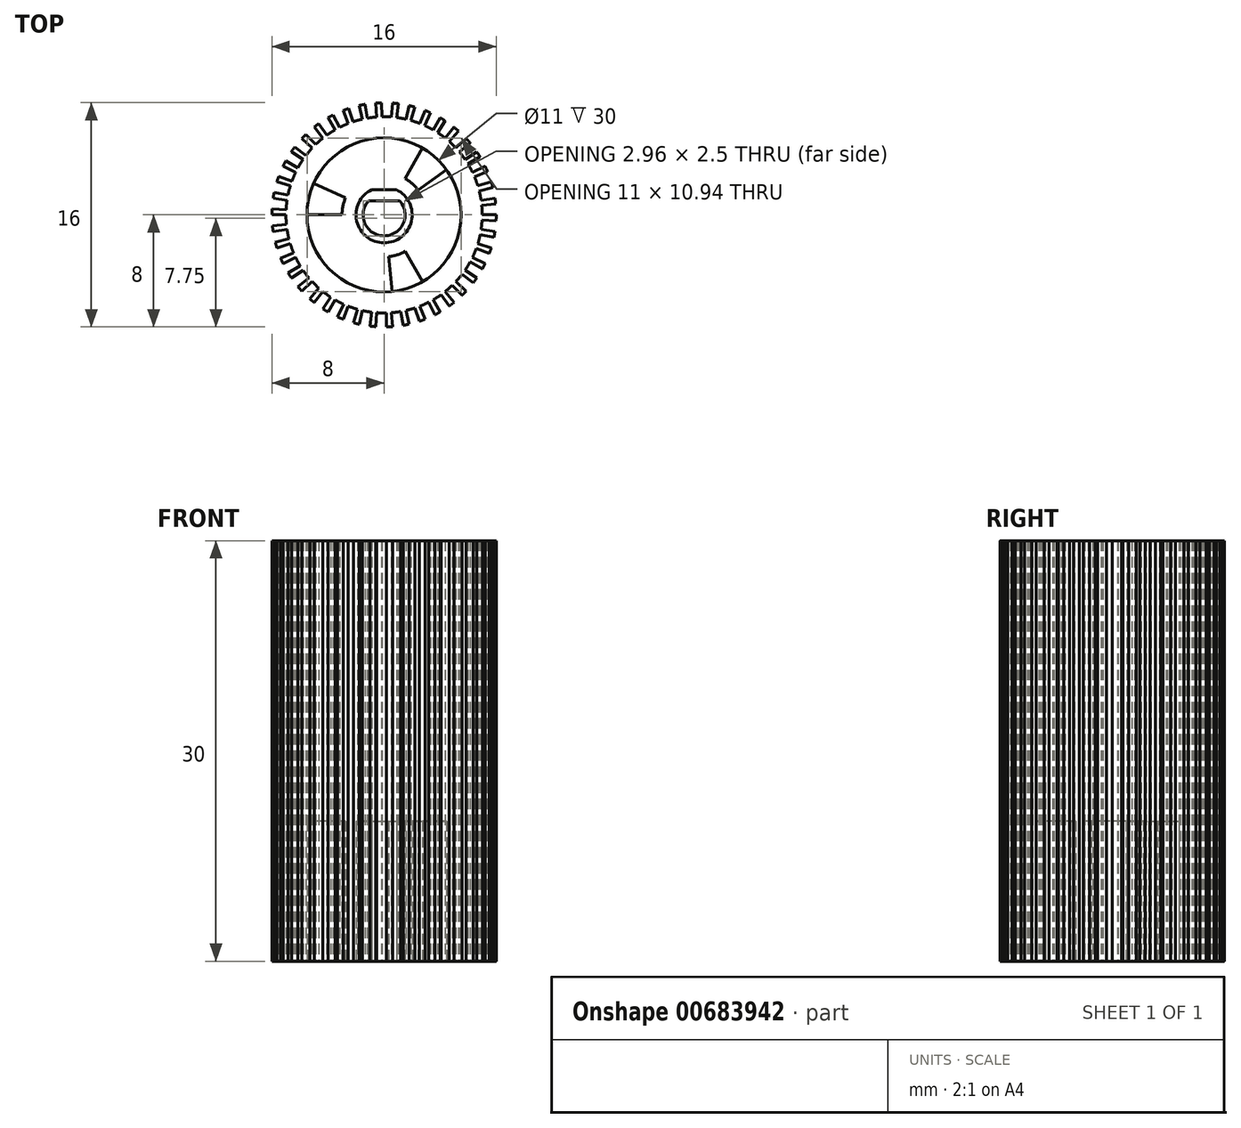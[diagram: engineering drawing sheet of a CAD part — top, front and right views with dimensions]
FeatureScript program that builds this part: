
annotation { "Feature Type Name" : "Feature", "Feature Type Description" : "" }
export const myFeature = defineFeature(function(context is Context, id is Id, definition is map)
    precondition{}
    {
        {
            var Q0;
            Q0=qCreatedBy(makeId("Top.planeOp"),FACE);
            var sketch = newSketch(context, id + "F0", { "sketchPlane" : qUnion([Q0])});
            skCircle(sketch, "E0", {"center": v(0, 0) * mm, "radius": 5.5 * mm});
            skCircle(sketch, "E1.0", {"center": v(0, 0) * mm, "radius": 7 * mm});
            skArc(sketch, "E2.0", {"start": v(-7.99, 0.42) * mm, "mid": v(-8, 0.2) * mm, "end": v(-8, 0) * mm});
            skLineSegment(sketch, "E3.trimOffspring", {"start": v(-7, 0.37) * mm, "end": v(-7.99, 0.42) * mm});
            skLineSegment(sketch, "E4.trimOffspring", {"start": v(-7, 0) * mm, "end": v(-8, 0) * mm});
            skLineSegment(sketch, "E5.1.0", {"start": v(-6.97, -0.68) * mm, "end": v(-7.96, -0.78) * mm});
            skLineSegment(sketch, "E5.1.1", {"start": v(-6.92, -1.04) * mm, "end": v(-7.91, -1.2) * mm});
            skArc(sketch, "E5.1.2", {"start": v(-7.96, -0.78) * mm, "mid": v(-7.94, -0.98) * mm, "end": v(-7.91, -1.2) * mm});
            skLineSegment(sketch, "E5.2.0", {"start": v(-6.79, -1.71) * mm, "end": v(-7.76, -1.95) * mm});
            skLineSegment(sketch, "E5.2.1", {"start": v(-6.69, -2.06) * mm, "end": v(-7.64, -2.36) * mm});
            skArc(sketch, "E5.2.2", {"start": v(-7.76, -1.95) * mm, "mid": v(-7.7, -2.16) * mm, "end": v(-7.64, -2.36) * mm});
            skLineSegment(sketch, "E5.3.0", {"start": v(-6.46, -2.7) * mm, "end": v(-7.38, -3.09) * mm});
            skLineSegment(sketch, "E5.3.1", {"start": v(-6.3, -3.04) * mm, "end": v(-7.2, -3.47) * mm});
            skArc(sketch, "E5.3.2", {"start": v(-7.38, -3.09) * mm, "mid": v(-7.3, -3.28) * mm, "end": v(-7.2, -3.47) * mm});
            skLineSegment(sketch, "E5.4.0", {"start": v(-5.98, -3.64) * mm, "end": v(-6.84, -4.15) * mm});
            skLineSegment(sketch, "E5.4.1", {"start": v(-5.78, -3.94) * mm, "end": v(-6.6, -4.5) * mm});
            skArc(sketch, "E5.4.2", {"start": v(-6.84, -4.15) * mm, "mid": v(-6.73, -4.33) * mm, "end": v(-6.6, -4.5) * mm});
            skLineSegment(sketch, "E5.5.0", {"start": v(-5.37, -4.49) * mm, "end": v(-6.14, -5.13) * mm});
            skLineSegment(sketch, "E5.5.1", {"start": v(-5.13, -4.76) * mm, "end": v(-5.86, -5.44) * mm});
            skArc(sketch, "E5.5.2", {"start": v(-6.14, -5.13) * mm, "mid": v(-6, -5.29) * mm, "end": v(-5.86, -5.44) * mm});
            skLineSegment(sketch, "E5.6.0", {"start": v(-4.64, -5.24) * mm, "end": v(-5.3, -5.99) * mm});
            skLineSegment(sketch, "E5.6.1", {"start": v(-4.36, -5.47) * mm, "end": v(-4.99, -6.25) * mm});
            skArc(sketch, "E5.6.2", {"start": v(-5.3, -5.99) * mm, "mid": v(-5.15, -6.12) * mm, "end": v(-4.99, -6.25) * mm});
            skLineSegment(sketch, "E5.7.0", {"start": v(-3.81, -5.87) * mm, "end": v(-4.36, -6.7) * mm});
            skLineSegment(sketch, "E5.7.1", {"start": v(-3.5, -6.06) * mm, "end": v(-4, -6.93) * mm});
            skArc(sketch, "E5.7.2", {"start": v(-4.36, -6.7) * mm, "mid": v(-4.18, -6.82) * mm, "end": v(-4, -6.93) * mm});
            skLineSegment(sketch, "E5.8.0", {"start": v(-2.9, -6.37) * mm, "end": v(-3.3, -7.28) * mm});
            skLineSegment(sketch, "E5.8.1", {"start": v(-2.56, -6.52) * mm, "end": v(-2.92, -7.45) * mm});
            skArc(sketch, "E5.8.2", {"start": v(-3.3, -7.28) * mm, "mid": v(-3.12, -7.37) * mm, "end": v(-2.92, -7.45) * mm});
            skLineSegment(sketch, "E5.9.0", {"start": v(-1.91, -6.73) * mm, "end": v(-2.19, -7.7) * mm});
            skLineSegment(sketch, "E5.9.1", {"start": v(-1.56, -6.82) * mm, "end": v(-1.78, -7.8) * mm});
            skArc(sketch, "E5.9.2", {"start": v(-2.19, -7.7) * mm, "mid": v(-1.98, -7.75) * mm, "end": v(-1.78, -7.8) * mm});
            skLineSegment(sketch, "E5.10.0", {"start": v(-0.89, -6.94) * mm, "end": v(-1.01, -7.94) * mm});
            skLineSegment(sketch, "E5.10.1", {"start": v(-0.52, -6.98) * mm, "end": v(-0.6, -7.98) * mm});
            skArc(sketch, "E5.10.2", {"start": v(-1.01, -7.94) * mm, "mid": v(-0.8, -7.96) * mm, "end": v(-0.6, -7.98) * mm});
            skLineSegment(sketch, "E5.11.0", {"start": v(0.16, -7) * mm, "end": v(0.18, -8) * mm});
            skLineSegment(sketch, "E5.11.1", {"start": v(0.52, -6.98) * mm, "end": v(0.6, -7.98) * mm});
            skArc(sketch, "E5.11.2", {"start": v(0.18, -8) * mm, "mid": v(0.39, -8) * mm, "end": v(0.6, -7.98) * mm});
            skLineSegment(sketch, "E5.12.0", {"start": v(1.2, -6.9) * mm, "end": v(1.37, -7.88) * mm});
            skLineSegment(sketch, "E5.12.1", {"start": v(1.56, -6.82) * mm, "end": v(1.78, -7.8) * mm});
            skArc(sketch, "E5.12.2", {"start": v(1.37, -7.88) * mm, "mid": v(1.58, -7.84) * mm, "end": v(1.78, -7.8) * mm});
            skLineSegment(sketch, "E5.13.0", {"start": v(2.21, -6.64) * mm, "end": v(2.53, -7.59) * mm});
            skLineSegment(sketch, "E5.13.1", {"start": v(2.56, -6.52) * mm, "end": v(2.92, -7.45) * mm});
            skArc(sketch, "E5.13.2", {"start": v(2.53, -7.59) * mm, "mid": v(2.73, -7.52) * mm, "end": v(2.92, -7.45) * mm});
            skLineSegment(sketch, "E5.14.0", {"start": v(3.18, -6.24) * mm, "end": v(3.63, -7.13) * mm});
            skLineSegment(sketch, "E5.14.1", {"start": v(3.5, -6.06) * mm, "end": v(4, -6.93) * mm});
            skArc(sketch, "E5.14.2", {"start": v(3.63, -7.13) * mm, "mid": v(3.82, -7.03) * mm, "end": v(4, -6.93) * mm});
            skLineSegment(sketch, "E5.15.0", {"start": v(4.07, -5.7) * mm, "end": v(4.65, -6.5) * mm});
            skLineSegment(sketch, "E5.15.1", {"start": v(4.36, -5.47) * mm, "end": v(4.99, -6.25) * mm});
            skArc(sketch, "E5.15.2", {"start": v(4.65, -6.5) * mm, "mid": v(4.82, -6.38) * mm, "end": v(4.99, -6.25) * mm});
            skLineSegment(sketch, "E5.16.0", {"start": v(4.88, -5.02) * mm, "end": v(5.57, -5.74) * mm});
            skLineSegment(sketch, "E5.16.1", {"start": v(5.13, -4.76) * mm, "end": v(5.86, -5.44) * mm});
            skArc(sketch, "E5.16.2", {"start": v(5.57, -5.74) * mm, "mid": v(5.72, -5.6) * mm, "end": v(5.86, -5.44) * mm});
            skLineSegment(sketch, "E5.17.0", {"start": v(5.57, -4.24) * mm, "end": v(6.36, -4.85) * mm});
            skLineSegment(sketch, "E5.17.1", {"start": v(5.78, -3.94) * mm, "end": v(6.6, -4.5) * mm});
            skArc(sketch, "E5.17.2", {"start": v(6.36, -4.85) * mm, "mid": v(6.49, -4.68) * mm, "end": v(6.6, -4.5) * mm});
            skLineSegment(sketch, "E5.18.0", {"start": v(6.14, -3.36) * mm, "end": v(7.02, -3.84) * mm});
            skLineSegment(sketch, "E5.18.1", {"start": v(6.3, -3.04) * mm, "end": v(7.2, -3.47) * mm});
            skArc(sketch, "E5.18.2", {"start": v(7.02, -3.84) * mm, "mid": v(7.11, -3.66) * mm, "end": v(7.2, -3.47) * mm});
            skLineSegment(sketch, "E5.19.0", {"start": v(6.57, -2.41) * mm, "end": v(7.51, -2.75) * mm});
            skLineSegment(sketch, "E5.19.1", {"start": v(6.69, -2.06) * mm, "end": v(7.64, -2.36) * mm});
            skArc(sketch, "E5.19.2", {"start": v(7.51, -2.75) * mm, "mid": v(7.58, -2.56) * mm, "end": v(7.64, -2.36) * mm});
            skLineSegment(sketch, "E5.20.0", {"start": v(6.86, -1.4) * mm, "end": v(7.84, -1.6) * mm});
            skLineSegment(sketch, "E5.20.1", {"start": v(6.92, -1.04) * mm, "end": v(7.91, -1.2) * mm});
            skArc(sketch, "E5.20.2", {"start": v(7.84, -1.6) * mm, "mid": v(7.88, -1.4) * mm, "end": v(7.91, -1.2) * mm});
            skLineSegment(sketch, "E5.21.0", {"start": v(7, -0.37) * mm, "end": v(7.99, -0.42) * mm});
            skLineSegment(sketch, "E5.21.1", {"start": v(7, 0) * mm, "end": v(8, 0) * mm});
            skArc(sketch, "E5.21.2", {"start": v(7.99, -0.42) * mm, "mid": v(8, -0.2) * mm, "end": v(8, 0) * mm});
            skLineSegment(sketch, "E5.22.0", {"start": v(6.97, 0.68) * mm, "end": v(7.96, 0.78) * mm});
            skLineSegment(sketch, "E5.22.1", {"start": v(6.92, 1.04) * mm, "end": v(7.91, 1.2) * mm});
            skArc(sketch, "E5.22.2", {"start": v(7.96, 0.78) * mm, "mid": v(7.94, 0.98) * mm, "end": v(7.91, 1.2) * mm});
            skLineSegment(sketch, "E5.23.0", {"start": v(6.79, 1.71) * mm, "end": v(7.76, 1.95) * mm});
            skLineSegment(sketch, "E5.23.1", {"start": v(6.69, 2.06) * mm, "end": v(7.64, 2.36) * mm});
            skArc(sketch, "E5.23.2", {"start": v(7.76, 1.95) * mm, "mid": v(7.7, 2.16) * mm, "end": v(7.64, 2.36) * mm});
            skLineSegment(sketch, "E5.24.0", {"start": v(6.46, 2.7) * mm, "end": v(7.38, 3.09) * mm});
            skLineSegment(sketch, "E5.24.1", {"start": v(6.3, 3.04) * mm, "end": v(7.2, 3.47) * mm});
            skArc(sketch, "E5.24.2", {"start": v(7.38, 3.09) * mm, "mid": v(7.3, 3.28) * mm, "end": v(7.2, 3.47) * mm});
            skLineSegment(sketch, "E5.25.0", {"start": v(5.98, 3.64) * mm, "end": v(6.84, 4.15) * mm});
            skLineSegment(sketch, "E5.25.1", {"start": v(5.78, 3.94) * mm, "end": v(6.6, 4.5) * mm});
            skArc(sketch, "E5.25.2", {"start": v(6.84, 4.15) * mm, "mid": v(6.73, 4.33) * mm, "end": v(6.6, 4.5) * mm});
            skLineSegment(sketch, "E5.26.0", {"start": v(5.37, 4.49) * mm, "end": v(6.14, 5.13) * mm});
            skLineSegment(sketch, "E5.26.1", {"start": v(5.13, 4.76) * mm, "end": v(5.86, 5.44) * mm});
            skArc(sketch, "E5.26.2", {"start": v(6.14, 5.13) * mm, "mid": v(6, 5.29) * mm, "end": v(5.86, 5.44) * mm});
            skLineSegment(sketch, "E5.27.0", {"start": v(4.64, 5.24) * mm, "end": v(5.3, 5.99) * mm});
            skLineSegment(sketch, "E5.27.1", {"start": v(4.36, 5.47) * mm, "end": v(4.99, 6.25) * mm});
            skArc(sketch, "E5.27.2", {"start": v(5.3, 5.99) * mm, "mid": v(5.15, 6.12) * mm, "end": v(4.99, 6.25) * mm});
            skLineSegment(sketch, "E5.28.0", {"start": v(3.81, 5.87) * mm, "end": v(4.36, 6.7) * mm});
            skLineSegment(sketch, "E5.28.1", {"start": v(3.5, 6.06) * mm, "end": v(4, 6.93) * mm});
            skArc(sketch, "E5.28.2", {"start": v(4.36, 6.7) * mm, "mid": v(4.18, 6.82) * mm, "end": v(4, 6.93) * mm});
            skLineSegment(sketch, "E5.29.0", {"start": v(2.9, 6.37) * mm, "end": v(3.3, 7.28) * mm});
            skLineSegment(sketch, "E5.29.1", {"start": v(2.56, 6.52) * mm, "end": v(2.92, 7.45) * mm});
            skArc(sketch, "E5.29.2", {"start": v(3.3, 7.28) * mm, "mid": v(3.12, 7.37) * mm, "end": v(2.92, 7.45) * mm});
            skLineSegment(sketch, "E5.30.0", {"start": v(1.91, 6.73) * mm, "end": v(2.19, 7.7) * mm});
            skLineSegment(sketch, "E5.30.1", {"start": v(1.56, 6.82) * mm, "end": v(1.78, 7.8) * mm});
            skArc(sketch, "E5.30.2", {"start": v(2.19, 7.7) * mm, "mid": v(1.98, 7.75) * mm, "end": v(1.78, 7.8) * mm});
            skLineSegment(sketch, "E5.31.0", {"start": v(0.89, 6.94) * mm, "end": v(1.01, 7.94) * mm});
            skLineSegment(sketch, "E5.31.1", {"start": v(0.52, 6.98) * mm, "end": v(0.6, 7.98) * mm});
            skArc(sketch, "E5.31.2", {"start": v(1.01, 7.94) * mm, "mid": v(0.8, 7.96) * mm, "end": v(0.6, 7.98) * mm});
            skLineSegment(sketch, "E5.32.0", {"start": v(-0.16, 7) * mm, "end": v(-0.18, 8) * mm});
            skLineSegment(sketch, "E5.32.1", {"start": v(-0.52, 6.98) * mm, "end": v(-0.6, 7.98) * mm});
            skArc(sketch, "E5.32.2", {"start": v(-0.18, 8) * mm, "mid": v(-0.39, 8) * mm, "end": v(-0.6, 7.98) * mm});
            skLineSegment(sketch, "E5.33.0", {"start": v(-1.2, 6.9) * mm, "end": v(-1.37, 7.88) * mm});
            skLineSegment(sketch, "E5.33.1", {"start": v(-1.56, 6.82) * mm, "end": v(-1.78, 7.8) * mm});
            skArc(sketch, "E5.33.2", {"start": v(-1.37, 7.88) * mm, "mid": v(-1.58, 7.84) * mm, "end": v(-1.78, 7.8) * mm});
            skLineSegment(sketch, "E5.34.0", {"start": v(-2.21, 6.64) * mm, "end": v(-2.53, 7.59) * mm});
            skLineSegment(sketch, "E5.34.1", {"start": v(-2.56, 6.52) * mm, "end": v(-2.92, 7.45) * mm});
            skArc(sketch, "E5.34.2", {"start": v(-2.53, 7.59) * mm, "mid": v(-2.73, 7.52) * mm, "end": v(-2.92, 7.45) * mm});
            skLineSegment(sketch, "E5.35.0", {"start": v(-3.18, 6.24) * mm, "end": v(-3.63, 7.13) * mm});
            skLineSegment(sketch, "E5.35.1", {"start": v(-3.5, 6.06) * mm, "end": v(-4, 6.93) * mm});
            skArc(sketch, "E5.35.2", {"start": v(-3.63, 7.13) * mm, "mid": v(-3.82, 7.03) * mm, "end": v(-4, 6.93) * mm});
            skLineSegment(sketch, "E5.36.0", {"start": v(-4.07, 5.7) * mm, "end": v(-4.65, 6.5) * mm});
            skLineSegment(sketch, "E5.36.1", {"start": v(-4.36, 5.47) * mm, "end": v(-4.99, 6.25) * mm});
            skArc(sketch, "E5.36.2", {"start": v(-4.65, 6.5) * mm, "mid": v(-4.82, 6.38) * mm, "end": v(-4.99, 6.25) * mm});
            skLineSegment(sketch, "E5.37.0", {"start": v(-4.88, 5.02) * mm, "end": v(-5.57, 5.74) * mm});
            skLineSegment(sketch, "E5.37.1", {"start": v(-5.13, 4.76) * mm, "end": v(-5.86, 5.44) * mm});
            skArc(sketch, "E5.37.2", {"start": v(-5.57, 5.74) * mm, "mid": v(-5.72, 5.6) * mm, "end": v(-5.86, 5.44) * mm});
            skLineSegment(sketch, "E5.38.0", {"start": v(-5.57, 4.24) * mm, "end": v(-6.36, 4.85) * mm});
            skLineSegment(sketch, "E5.38.1", {"start": v(-5.78, 3.94) * mm, "end": v(-6.6, 4.5) * mm});
            skArc(sketch, "E5.38.2", {"start": v(-6.36, 4.85) * mm, "mid": v(-6.49, 4.68) * mm, "end": v(-6.6, 4.5) * mm});
            skLineSegment(sketch, "E5.39.0", {"start": v(-6.14, 3.36) * mm, "end": v(-7.02, 3.84) * mm});
            skLineSegment(sketch, "E5.39.1", {"start": v(-6.3, 3.04) * mm, "end": v(-7.2, 3.47) * mm});
            skArc(sketch, "E5.39.2", {"start": v(-7.02, 3.84) * mm, "mid": v(-7.11, 3.66) * mm, "end": v(-7.2, 3.47) * mm});
            skLineSegment(sketch, "E5.40.0", {"start": v(-6.57, 2.41) * mm, "end": v(-7.51, 2.75) * mm});
            skLineSegment(sketch, "E5.40.1", {"start": v(-6.69, 2.06) * mm, "end": v(-7.64, 2.36) * mm});
            skArc(sketch, "E5.40.2", {"start": v(-7.51, 2.75) * mm, "mid": v(-7.58, 2.56) * mm, "end": v(-7.64, 2.36) * mm});
            skLineSegment(sketch, "E5.41.0", {"start": v(-6.86, 1.4) * mm, "end": v(-7.84, 1.6) * mm});
            skLineSegment(sketch, "E5.41.1", {"start": v(-6.92, 1.04) * mm, "end": v(-7.91, 1.2) * mm});
            skArc(sketch, "E5.41.2", {"start": v(-7.84, 1.6) * mm, "mid": v(-7.88, 1.4) * mm, "end": v(-7.91, 1.2) * mm});
            skArc(sketch, "E6", {"start": v(-1.12, 1) * mm, "mid": v(0, -1.5) * mm, "end": v(1.12, 1) * mm});
            skLineSegment(sketch, "E7", {"start": v(-1.12, 1) * mm, "end": v(1.12, 1) * mm});
            skCircle(sketch, "E8.0", {"center": v(0, 0) * mm, "radius": 3 * mm});
            skLineSegment(sketch, "E9.trimOffspring", {"start": v(-2.74, 1.22) * mm, "end": v(-5.02, 2.24) * mm});
            skLineSegment(sketch, "E10.trimOffspring", {"start": v(-3, 0) * mm, "end": v(-5.5, 0) * mm});
            skLineSegment(sketch, "E11.1.0", {"start": v(0.31, -2.98) * mm, "end": v(0.57, -5.47) * mm});
            skLineSegment(sketch, "E11.1.1", {"start": v(1.5, -2.6) * mm, "end": v(2.75, -4.76) * mm});
            skLineSegment(sketch, "E11.2.0", {"start": v(2.43, 1.76) * mm, "end": v(4.45, 3.23) * mm});
            skLineSegment(sketch, "E11.2.1", {"start": v(1.5, 2.6) * mm, "end": v(2.75, 4.76) * mm});
            skCircle(sketch, "E12", {"center": v(0, 0) * mm, "radius": 2 * mm});
            skLineSegment(sketch, "E13", {"start": v(-0.88, 1.8) * mm, "end": v(0.88, 1.8) * mm});
            skSolve(sketch);
        }
        {
            var Q0;
            {var subQ0=sQuery(id+"F0.wireOp",EDGE,"E10.trimOffspring");Q0=makeQuery(id+"F0.imprint","IMPRINT",FACE,{"disambiguationData":[TD([[makeQuery(id+"F0.imprint","IMPRINT",EDGE,{"derivedFrom":subQ0}),1.0]])]});}
            var Q1;
            {var subQ0=sQuery(id+"F0.wireOp",EDGE,"E9.trimOffspring");Q1=makeQuery(id+"F0.imprint","IMPRINT",FACE,{"disambiguationData":[TD([[makeQuery(id+"F0.imprint","IMPRINT",EDGE,{"derivedFrom":subQ0}),1.0]])]});}
            var Q2;
            {var subQ0=sQuery(id+"F0.wireOp",EDGE,"E9.trimOffspring");Q2=makeQuery(id+"F0.imprint","IMPRINT",FACE,{"disambiguationData":[TD([[makeQuery(id+"F0.imprint","IMPRINT",EDGE,{"derivedFrom":subQ0}),-1.0]])]});}
            var Q3;
            {var subQ0=sQuery(id+"F0.wireOp",EDGE,"E11.2.0");Q3=makeQuery(id+"F0.imprint","IMPRINT",FACE,{"disambiguationData":[TD([[makeQuery(id+"F0.imprint","IMPRINT",EDGE,{"derivedFrom":subQ0}),1.0]])]});}
            var Q4;
            {var subQ0=sQuery(id+"F0.wireOp",EDGE,"E11.1.1");Q4=makeQuery(id+"F0.imprint","IMPRINT",FACE,{"disambiguationData":[TD([[makeQuery(id+"F0.imprint","IMPRINT",EDGE,{"derivedFrom":subQ0}),1.0]])]});}
            var Q5;
            {var subQ0=sQuery(id+"F0.wireOp",EDGE,"E11.1.0");Q5=makeQuery(id+"F0.imprint","IMPRINT",FACE,{"disambiguationData":[TD([[makeQuery(id+"F0.imprint","IMPRINT",EDGE,{"derivedFrom":subQ0}),1.0]])]});}
            extrude(context, id + "F1", {"entities" : qUnion([Q0, Q1, Q2, Q3, Q4, Q5]), "depth" : 1.5 * mm, "offsetDistance" : 25 * mm});
        }
        {
            var Q0;
            {var subQ31=sQuery(id+"F0.wireOp",EDGE,"E0");var subQ33=makeQuery(id+"F0.imprint","INTERSECT",VERTEX,{"derivedFrom":[subQ31,sQuery(id+"F0.wireOp",EDGE,"E11.2.0")]});Q0=makeQuery(id+"F0.imprint","IMPRINT",FACE,{"disambiguationData":[TD([[makeQuery(id+"F0.imprint","IMPRINT",EDGE,{"disambiguationData":[TD([[subQ33,-1.0]])],"derivedFrom":subQ31}),-1.0]])]});}
            var Q1;
            {var subQ0=sQuery(id+"F0.wireOp",EDGE,"E5.38.0");Q1=makeQuery(id+"F0.imprint","IMPRINT",FACE,{"disambiguationData":[TD([[makeQuery(id+"F0.imprint","IMPRINT",EDGE,{"derivedFrom":subQ0}),1.0]])]});}
            var Q2;
            {var subQ0=sQuery(id+"F0.wireOp",EDGE,"E5.37.0");Q2=makeQuery(id+"F0.imprint","IMPRINT",FACE,{"disambiguationData":[TD([[makeQuery(id+"F0.imprint","IMPRINT",EDGE,{"derivedFrom":subQ0}),1.0]])]});}
            var Q3;
            {var subQ0=sQuery(id+"F0.wireOp",EDGE,"E5.36.0");Q3=makeQuery(id+"F0.imprint","IMPRINT",FACE,{"disambiguationData":[TD([[makeQuery(id+"F0.imprint","IMPRINT",EDGE,{"derivedFrom":subQ0}),1.0]])]});}
            var Q4;
            {var subQ0=sQuery(id+"F0.wireOp",EDGE,"E5.35.0");Q4=makeQuery(id+"F0.imprint","IMPRINT",FACE,{"disambiguationData":[TD([[makeQuery(id+"F0.imprint","IMPRINT",EDGE,{"derivedFrom":subQ0}),1.0]])]});}
            var Q5;
            {var subQ0=sQuery(id+"F0.wireOp",EDGE,"E5.34.0");Q5=makeQuery(id+"F0.imprint","IMPRINT",FACE,{"disambiguationData":[TD([[makeQuery(id+"F0.imprint","IMPRINT",EDGE,{"derivedFrom":subQ0}),1.0]])]});}
            var Q6;
            {var subQ0=sQuery(id+"F0.wireOp",EDGE,"E5.33.0");Q6=makeQuery(id+"F0.imprint","IMPRINT",FACE,{"disambiguationData":[TD([[makeQuery(id+"F0.imprint","IMPRINT",EDGE,{"derivedFrom":subQ0}),1.0]])]});}
            var Q7;
            {var subQ0=sQuery(id+"F0.wireOp",EDGE,"E5.32.0");Q7=makeQuery(id+"F0.imprint","IMPRINT",FACE,{"disambiguationData":[TD([[makeQuery(id+"F0.imprint","IMPRINT",EDGE,{"derivedFrom":subQ0}),1.0]])]});}
            var Q8;
            {var subQ0=sQuery(id+"F0.wireOp",EDGE,"E5.31.0");Q8=makeQuery(id+"F0.imprint","IMPRINT",FACE,{"disambiguationData":[TD([[makeQuery(id+"F0.imprint","IMPRINT",EDGE,{"derivedFrom":subQ0}),1.0]])]});}
            var Q9;
            {var subQ0=sQuery(id+"F0.wireOp",EDGE,"E5.30.0");Q9=makeQuery(id+"F0.imprint","IMPRINT",FACE,{"disambiguationData":[TD([[makeQuery(id+"F0.imprint","IMPRINT",EDGE,{"derivedFrom":subQ0}),1.0]])]});}
            var Q10;
            {var subQ0=sQuery(id+"F0.wireOp",EDGE,"E5.29.0");Q10=makeQuery(id+"F0.imprint","IMPRINT",FACE,{"disambiguationData":[TD([[makeQuery(id+"F0.imprint","IMPRINT",EDGE,{"derivedFrom":subQ0}),1.0]])]});}
            var Q11;
            {var subQ0=sQuery(id+"F0.wireOp",EDGE,"E5.28.0");Q11=makeQuery(id+"F0.imprint","IMPRINT",FACE,{"disambiguationData":[TD([[makeQuery(id+"F0.imprint","IMPRINT",EDGE,{"derivedFrom":subQ0}),1.0]])]});}
            var Q12;
            {var subQ0=sQuery(id+"F0.wireOp",EDGE,"E5.27.0");Q12=makeQuery(id+"F0.imprint","IMPRINT",FACE,{"disambiguationData":[TD([[makeQuery(id+"F0.imprint","IMPRINT",EDGE,{"derivedFrom":subQ0}),1.0]])]});}
            var Q13;
            {var subQ0=sQuery(id+"F0.wireOp",EDGE,"E5.26.0");Q13=makeQuery(id+"F0.imprint","IMPRINT",FACE,{"disambiguationData":[TD([[makeQuery(id+"F0.imprint","IMPRINT",EDGE,{"derivedFrom":subQ0}),1.0]])]});}
            var Q14;
            {var subQ0=sQuery(id+"F0.wireOp",EDGE,"E5.25.0");Q14=makeQuery(id+"F0.imprint","IMPRINT",FACE,{"disambiguationData":[TD([[makeQuery(id+"F0.imprint","IMPRINT",EDGE,{"derivedFrom":subQ0}),1.0]])]});}
            var Q15;
            {var subQ0=sQuery(id+"F0.wireOp",EDGE,"E5.24.0");Q15=makeQuery(id+"F0.imprint","IMPRINT",FACE,{"disambiguationData":[TD([[makeQuery(id+"F0.imprint","IMPRINT",EDGE,{"derivedFrom":subQ0}),1.0]])]});}
            var Q16;
            {var subQ0=sQuery(id+"F0.wireOp",EDGE,"E5.23.0");Q16=makeQuery(id+"F0.imprint","IMPRINT",FACE,{"disambiguationData":[TD([[makeQuery(id+"F0.imprint","IMPRINT",EDGE,{"derivedFrom":subQ0}),1.0]])]});}
            var Q17;
            {var subQ0=sQuery(id+"F0.wireOp",EDGE,"E5.22.0");Q17=makeQuery(id+"F0.imprint","IMPRINT",FACE,{"disambiguationData":[TD([[makeQuery(id+"F0.imprint","IMPRINT",EDGE,{"derivedFrom":subQ0}),1.0]])]});}
            var Q18;
            {var subQ0=sQuery(id+"F0.wireOp",EDGE,"E5.21.0");Q18=makeQuery(id+"F0.imprint","IMPRINT",FACE,{"disambiguationData":[TD([[makeQuery(id+"F0.imprint","IMPRINT",EDGE,{"derivedFrom":subQ0}),1.0]])]});}
            var Q19;
            {var subQ0=sQuery(id+"F0.wireOp",EDGE,"E5.20.0");Q19=makeQuery(id+"F0.imprint","IMPRINT",FACE,{"disambiguationData":[TD([[makeQuery(id+"F0.imprint","IMPRINT",EDGE,{"derivedFrom":subQ0}),1.0]])]});}
            var Q20;
            {var subQ0=sQuery(id+"F0.wireOp",EDGE,"E5.19.0");Q20=makeQuery(id+"F0.imprint","IMPRINT",FACE,{"disambiguationData":[TD([[makeQuery(id+"F0.imprint","IMPRINT",EDGE,{"derivedFrom":subQ0}),1.0]])]});}
            var Q21;
            {var subQ0=sQuery(id+"F0.wireOp",EDGE,"E5.18.0");Q21=makeQuery(id+"F0.imprint","IMPRINT",FACE,{"disambiguationData":[TD([[makeQuery(id+"F0.imprint","IMPRINT",EDGE,{"derivedFrom":subQ0}),1.0]])]});}
            var Q22;
            {var subQ0=sQuery(id+"F0.wireOp",EDGE,"E5.17.0");Q22=makeQuery(id+"F0.imprint","IMPRINT",FACE,{"disambiguationData":[TD([[makeQuery(id+"F0.imprint","IMPRINT",EDGE,{"derivedFrom":subQ0}),1.0]])]});}
            var Q23;
            {var subQ0=sQuery(id+"F0.wireOp",EDGE,"E5.16.0");Q23=makeQuery(id+"F0.imprint","IMPRINT",FACE,{"disambiguationData":[TD([[makeQuery(id+"F0.imprint","IMPRINT",EDGE,{"derivedFrom":subQ0}),1.0]])]});}
            var Q24;
            {var subQ0=sQuery(id+"F0.wireOp",EDGE,"E5.15.0");Q24=makeQuery(id+"F0.imprint","IMPRINT",FACE,{"disambiguationData":[TD([[makeQuery(id+"F0.imprint","IMPRINT",EDGE,{"derivedFrom":subQ0}),1.0]])]});}
            var Q25;
            {var subQ0=sQuery(id+"F0.wireOp",EDGE,"E5.14.0");Q25=makeQuery(id+"F0.imprint","IMPRINT",FACE,{"disambiguationData":[TD([[makeQuery(id+"F0.imprint","IMPRINT",EDGE,{"derivedFrom":subQ0}),1.0]])]});}
            var Q26;
            {var subQ0=sQuery(id+"F0.wireOp",EDGE,"E5.13.0");Q26=makeQuery(id+"F0.imprint","IMPRINT",FACE,{"disambiguationData":[TD([[makeQuery(id+"F0.imprint","IMPRINT",EDGE,{"derivedFrom":subQ0}),1.0]])]});}
            var Q27;
            {var subQ0=sQuery(id+"F0.wireOp",EDGE,"E5.12.0");Q27=makeQuery(id+"F0.imprint","IMPRINT",FACE,{"disambiguationData":[TD([[makeQuery(id+"F0.imprint","IMPRINT",EDGE,{"derivedFrom":subQ0}),1.0]])]});}
            var Q28;
            {var subQ0=sQuery(id+"F0.wireOp",EDGE,"E5.11.0");Q28=makeQuery(id+"F0.imprint","IMPRINT",FACE,{"disambiguationData":[TD([[makeQuery(id+"F0.imprint","IMPRINT",EDGE,{"derivedFrom":subQ0}),1.0]])]});}
            var Q29;
            {var subQ0=sQuery(id+"F0.wireOp",EDGE,"E5.10.0");Q29=makeQuery(id+"F0.imprint","IMPRINT",FACE,{"disambiguationData":[TD([[makeQuery(id+"F0.imprint","IMPRINT",EDGE,{"derivedFrom":subQ0}),1.0]])]});}
            var Q30;
            {var subQ0=sQuery(id+"F0.wireOp",EDGE,"E5.9.0");Q30=makeQuery(id+"F0.imprint","IMPRINT",FACE,{"disambiguationData":[TD([[makeQuery(id+"F0.imprint","IMPRINT",EDGE,{"derivedFrom":subQ0}),1.0]])]});}
            var Q31;
            {var subQ0=sQuery(id+"F0.wireOp",EDGE,"E5.8.0");Q31=makeQuery(id+"F0.imprint","IMPRINT",FACE,{"disambiguationData":[TD([[makeQuery(id+"F0.imprint","IMPRINT",EDGE,{"derivedFrom":subQ0}),1.0]])]});}
            var Q32;
            {var subQ0=sQuery(id+"F0.wireOp",EDGE,"E5.7.0");Q32=makeQuery(id+"F0.imprint","IMPRINT",FACE,{"disambiguationData":[TD([[makeQuery(id+"F0.imprint","IMPRINT",EDGE,{"derivedFrom":subQ0}),1.0]])]});}
            var Q33;
            {var subQ0=sQuery(id+"F0.wireOp",EDGE,"E5.6.0");Q33=makeQuery(id+"F0.imprint","IMPRINT",FACE,{"disambiguationData":[TD([[makeQuery(id+"F0.imprint","IMPRINT",EDGE,{"derivedFrom":subQ0}),1.0]])]});}
            var Q34;
            {var subQ0=sQuery(id+"F0.wireOp",EDGE,"E5.5.0");Q34=makeQuery(id+"F0.imprint","IMPRINT",FACE,{"disambiguationData":[TD([[makeQuery(id+"F0.imprint","IMPRINT",EDGE,{"derivedFrom":subQ0}),1.0]])]});}
            var Q35;
            {var subQ0=sQuery(id+"F0.wireOp",EDGE,"E5.4.0");Q35=makeQuery(id+"F0.imprint","IMPRINT",FACE,{"disambiguationData":[TD([[makeQuery(id+"F0.imprint","IMPRINT",EDGE,{"derivedFrom":subQ0}),1.0]])]});}
            var Q36;
            {var subQ0=sQuery(id+"F0.wireOp",EDGE,"E5.3.0");Q36=makeQuery(id+"F0.imprint","IMPRINT",FACE,{"disambiguationData":[TD([[makeQuery(id+"F0.imprint","IMPRINT",EDGE,{"derivedFrom":subQ0}),1.0]])]});}
            var Q37;
            {var subQ0=sQuery(id+"F0.wireOp",EDGE,"E5.2.0");Q37=makeQuery(id+"F0.imprint","IMPRINT",FACE,{"disambiguationData":[TD([[makeQuery(id+"F0.imprint","IMPRINT",EDGE,{"derivedFrom":subQ0}),1.0]])]});}
            var Q38;
            {var subQ0=sQuery(id+"F0.wireOp",EDGE,"E5.1.0");Q38=makeQuery(id+"F0.imprint","IMPRINT",FACE,{"disambiguationData":[TD([[makeQuery(id+"F0.imprint","IMPRINT",EDGE,{"derivedFrom":subQ0}),1.0]])]});}
            var Q39;
            Q39=makeQuery(id+"F0.imprint","IMPRINT",FACE,{"disambiguationData":[TD([[makeQuery(id+"F0.imprint","IMPRINT",EDGE,{"derivedFrom":sQuery(id+"F0.wireOp",EDGE,"E2.0")}),1.0]])]});
            var Q40;
            {var subQ0=sQuery(id+"F0.wireOp",EDGE,"E5.41.0");Q40=makeQuery(id+"F0.imprint","IMPRINT",FACE,{"disambiguationData":[TD([[makeQuery(id+"F0.imprint","IMPRINT",EDGE,{"derivedFrom":subQ0}),1.0]])]});}
            var Q41;
            {var subQ0=sQuery(id+"F0.wireOp",EDGE,"E5.40.0");Q41=makeQuery(id+"F0.imprint","IMPRINT",FACE,{"disambiguationData":[TD([[makeQuery(id+"F0.imprint","IMPRINT",EDGE,{"derivedFrom":subQ0}),1.0]])]});}
            var Q42;
            {var subQ0=sQuery(id+"F0.wireOp",EDGE,"E5.39.0");Q42=makeQuery(id+"F0.imprint","IMPRINT",FACE,{"disambiguationData":[TD([[makeQuery(id+"F0.imprint","IMPRINT",EDGE,{"derivedFrom":subQ0}),1.0]])]});}
            extrude(context, id + "F2", {"entities" : qUnion([Q0, Q1, Q2, Q3, Q4, Q5, Q6, Q7, Q8, Q9, Q10, Q11, Q12, Q13, Q14, Q15, Q16, Q17, Q18, Q19, Q20, Q21, Q22, Q23, Q24, Q25, Q26, Q27, Q28, Q29, Q30, Q31, Q32, Q33, Q34, Q35, Q36, Q37, Q38, Q39, Q40, Q41, Q42]), "operationType" : NewBodyOperationType.ADD, "depth" : 30 * mm, "offsetDistance" : 25 * mm});
        }
        {
            var Q0;
            Q0=makeQuery(id+"F0.imprint","IMPRINT",FACE,{"disambiguationData":[TD([[makeQuery(id+"F0.imprint","IMPRINT",EDGE,{"derivedFrom":sQuery(id+"F0.wireOp",EDGE,"E6")}),-1.0]])]});
            extrude(context, id + "F3", {"entities" : qUnion([Q0]), "operationType" : NewBodyOperationType.ADD, "depth" : 10 * mm, "offsetDistance" : 25 * mm});
        }
        {
            var Q0;
            {var subQ0=sQuery(id+"F0.wireOp",EDGE,"E9.trimOffspring");Q0=makeQuery(id+"F0.imprint","IMPRINT",FACE,{"disambiguationData":[TD([[makeQuery(id+"F0.imprint","IMPRINT",EDGE,{"derivedFrom":subQ0}),1.0]])]});}
            var Q1;
            {var subQ0=sQuery(id+"F0.wireOp",EDGE,"E11.2.0");Q1=makeQuery(id+"F0.imprint","IMPRINT",FACE,{"disambiguationData":[TD([[makeQuery(id+"F0.imprint","IMPRINT",EDGE,{"derivedFrom":subQ0}),1.0]])]});}
            var Q2;
            {var subQ0=sQuery(id+"F0.wireOp",EDGE,"E11.1.0");Q2=makeQuery(id+"F0.imprint","IMPRINT",FACE,{"disambiguationData":[TD([[makeQuery(id+"F0.imprint","IMPRINT",EDGE,{"derivedFrom":subQ0}),1.0]])]});}
            extrude(context, id + "F4", {"entities" : qUnion([Q0, Q1, Q2]), "operationType" : NewBodyOperationType.ADD, "depth" : 10 * mm, "offsetDistance" : 25 * mm});
        }
        {
            var Q0;
            {var subQ0=sQuery(id+"F0.wireOp",EDGE,"E11.1.1");Q0=makeQuery(id+"F0.imprint","IMPRINT",FACE,{"disambiguationData":[TD([[makeQuery(id+"F0.imprint","IMPRINT",EDGE,{"derivedFrom":subQ0}),1.0]])]});}
            var Q1;
            {var subQ0=sQuery(id+"F0.wireOp",EDGE,"E10.trimOffspring");Q1=makeQuery(id+"F0.imprint","IMPRINT",FACE,{"disambiguationData":[TD([[makeQuery(id+"F0.imprint","IMPRINT",EDGE,{"derivedFrom":subQ0}),1.0]])]});}
            var Q2;
            {var subQ0=sQuery(id+"F0.wireOp",EDGE,"E9.trimOffspring");Q2=makeQuery(id+"F0.imprint","IMPRINT",FACE,{"disambiguationData":[TD([[makeQuery(id+"F0.imprint","IMPRINT",EDGE,{"derivedFrom":subQ0}),-1.0]])]});}
            extrude(context, id + "F5", {"entities" : qUnion([Q0, Q1, Q2]), "operationType" : NewBodyOperationType.REMOVE, "oppositeDirection" : true, "depth" : -1.5 * mm, "offsetDistance" : 25 * mm});
        }
    });
